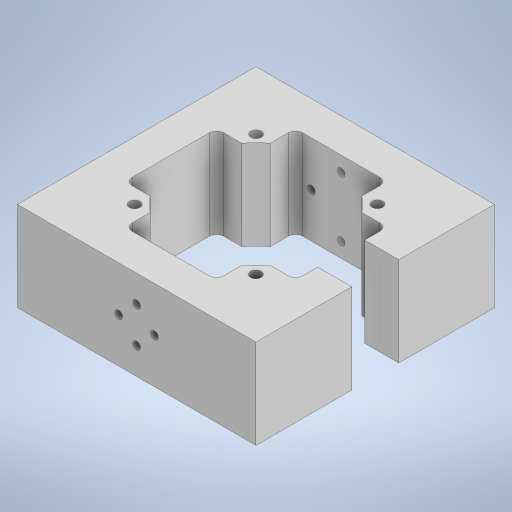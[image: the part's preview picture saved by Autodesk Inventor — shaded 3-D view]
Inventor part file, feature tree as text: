
AUTODESK INVENTOR PART (.ipt)
format: ipt  version: 2024 (Build 280153000, 153)  size: 385,536 bytes
history: native  units: in
note: dims shown in document units (in); Inventor stores cm internally (conversion verified against a paired STEP export)
features: extrude x8, sketch x8, fillet x1
ambient origin geometry x8: Origin, YZ Plane, XZ Plane, XY Plane, X Axis, Y Axis, Z Axis, Center Point
bodies: Body1 (feature_tree)
feature tree (17):
  extrude  "Extrusion15"  Depth=8.0in
  extrude  "Extrusion16"  Depth=3.0in
  extrude  "Extrusion17"  Depth=1.4409in
  sketch  "Sketch19"  dims[d156=1.4409in d157=0.0in d158=0.0in]
  sketch  "Sketch22"  dims[d159=4.0in d160=1.5in]
  extrude  "Extrusion20"  TaperAngle=0.0deg  [1 undecoded]
  extrude  "Extrusion28"  Depth=1.5in
  extrude  "Extrusion29"  Depth=0.25in
  extrude  "Extrusion30"  Depth=1.5748in TaperAngle=360.0deg
  fillet  "Fillet9"  Radius=4.0in
  extrude  "Extrusion31"  Depth=0.25in
  sketch  "Sketch15"  dims[d149=8.0in d150=8.0in]
  sketch  "Sketch16"  dims[d151=3.0in d152=0.0in d153=5.1181in]
  sketch  "Sketch17"  dims[d154=5.1181in d155=1.4409in]
  sketch  "Sketch23"  dims[d161=0.25in d162=0.6in]
  sketch  "Sketch26"  dims[d163=0.0in d164=1.5748in d166=360.0deg d168=4.0in d169=0.0in]
  sketch  "Sketch28"  dims[d170=1.5748in d171=1.7717in d172=1.445in d180=4.0in d181=1.5in d182=1.0in d183=0.0in d184=0.25in d185=1.5748in d187=360.0deg d189=4.0in d190=0.0in d191=1.0236in d206=0.5467in d207=0.5467in d208=2.6in d209=1.0236in d210=0.5256in d214=0.354in d217=0.5026in d218=1.0236in d219=1.0236in d220=0.5467in d221=0.5467in d222=2.6in d223=0.354in d224=0.5026in d225=0.5256in d232=90.0deg d233=1.0236in d234=2.5591in d235=5.1181in d236=0.0in d237=3.0in d238=0.0in d242=0.0in d243=0.3in d244=0.0in d245=0.3in d246=0.0in d247=0.0in d253=0.0in d254=0.3in d255=0.0in d256=0.3in d257=0.0in d258=0.0in d259=0.25in d260=0.0in d261=0.0in d28=0.0in d29=0.0in d30=0.0in d31=0.0in d144=0.0197in d145=0.0344in d146=0.0197in d147=0.0344in d192=0.0344in d212=0.5in d213=0.0344in d215=0.0344in d262=0.5in d263=0.0344in]
note: 1 required parameter value undecoded (feature->parameter linkage not recoverable at this tier; creation-order binding heuristic only, values carry confidence <= 0.55)
